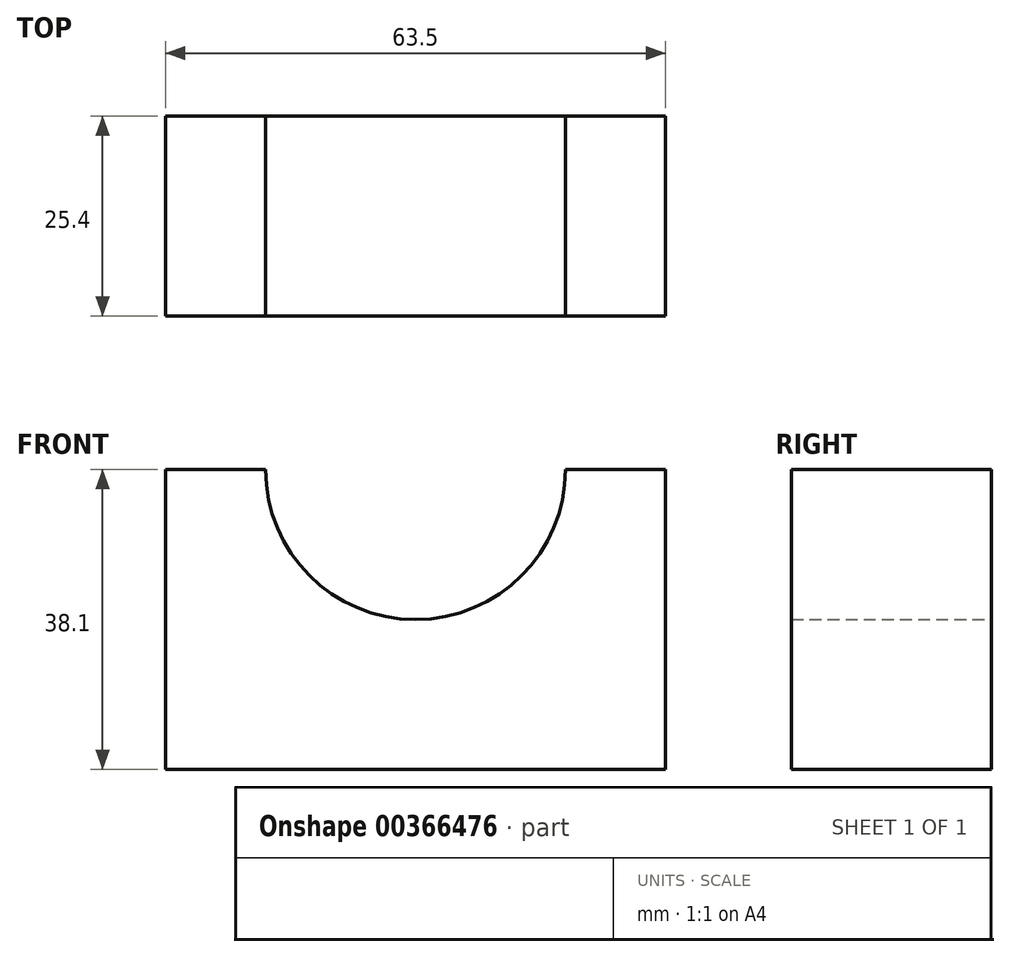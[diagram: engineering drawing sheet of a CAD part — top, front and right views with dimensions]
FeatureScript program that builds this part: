
annotation { "Feature Type Name" : "Feature", "Feature Type Description" : "" }
export const myFeature = defineFeature(function(context is Context, id is Id, definition is map)
    precondition{}
    {
        {
            var Q0;
            Q0=qCreatedBy(makeId("Front.planeOp"),FACE);
            var sketch = newSketch(context, id + "F0", { "sketchPlane" : qUnion([Q0])});
            skLineSegment(sketch, "E0", {"start": v(0, 0) * mm, "end": v(0, 38.1) * mm});
            skLineSegment(sketch, "E1", {"start": v(0, 38.1) * mm, "end": v(12.7, 38.1) * mm});
            skLineSegment(sketch, "E2", {"start": v(0, 0) * mm, "end": v(63.5, 0) * mm});
            skLineSegment(sketch, "E3", {"start": v(63.5, 0) * mm, "end": v(63.5, 38.1) * mm});
            skLineSegment(sketch, "E4", {"start": v(63.5, 38.1) * mm, "end": v(50.8, 38.1) * mm});
            skArc(sketch, "E5", {"start": v(12.7, 38.1) * mm, "mid": v(31.75, 19.05) * mm, "end": v(50.8, 38.1) * mm});
            skSolve(sketch);
        }
        {
            var Q0;
            Q0 = qSketchRegion(id + "F0", true);
            extrude(context, id + "F1", {"entities" : qUnion([Q0]), "depth" : 25.4 * mm});
        }
    });
